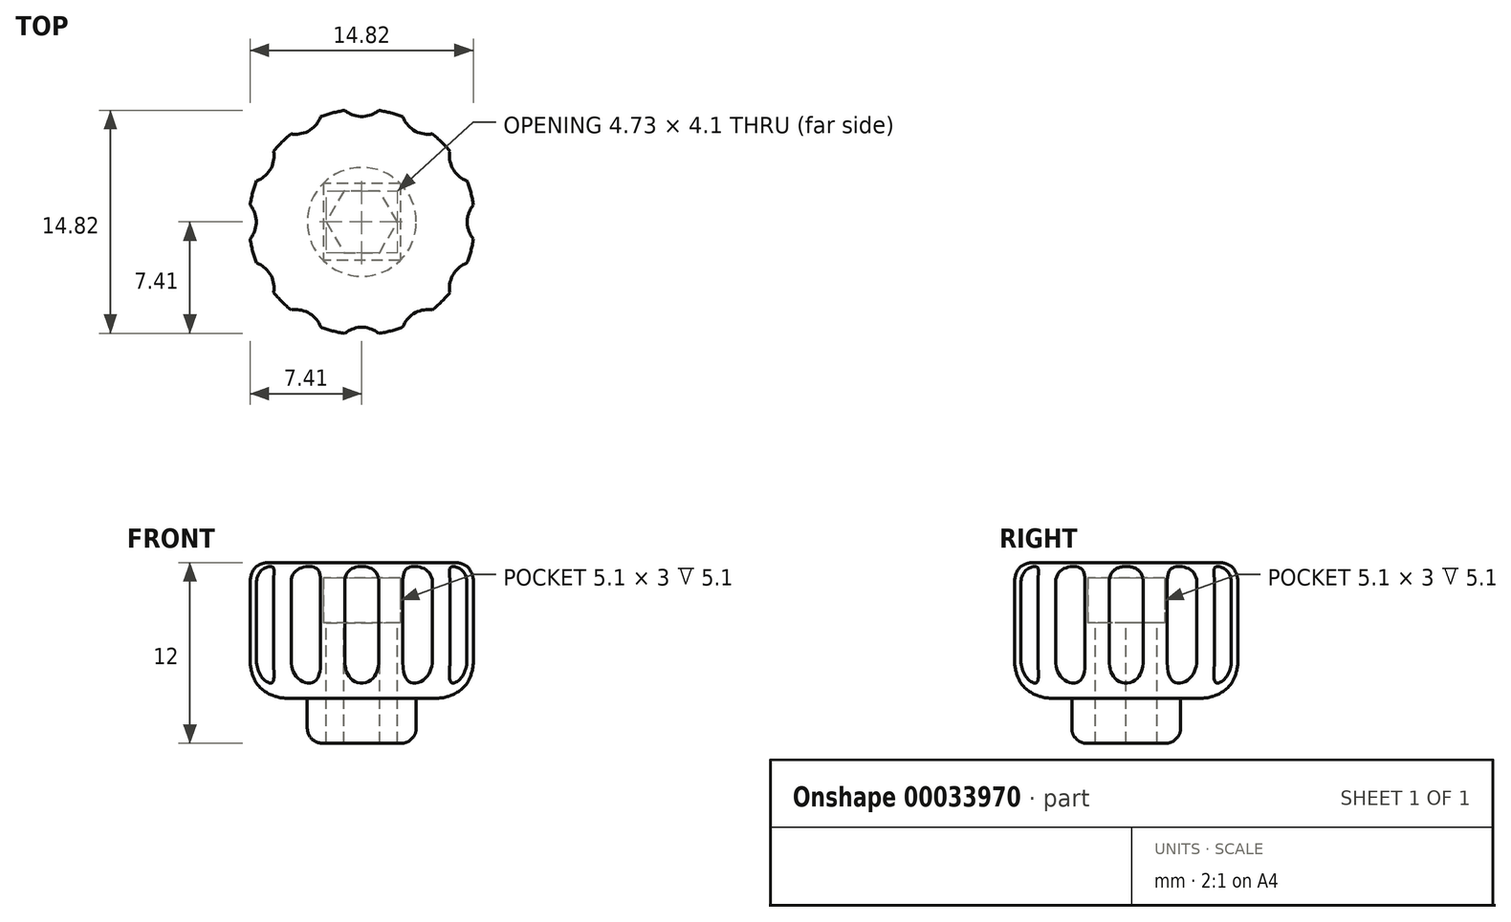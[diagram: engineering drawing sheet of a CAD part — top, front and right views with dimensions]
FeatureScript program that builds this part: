
annotation { "Feature Type Name" : "Feature", "Feature Type Description" : "" }
export const myFeature = defineFeature(function(context is Context, id is Id, definition is map)
    precondition{}
    {
        {
            var Q0;
            Q0=qCreatedBy(makeId("Top.planeOp"),FACE);
            var sketch = newSketch(context, id + "F0", { "sketchPlane" : qUnion([Q0])});
            skCircle(sketch, "E0", {"center": v(0, 0) * mm, "radius": 7.5 * mm});
            skLineSegment(sketch, "E1.rect.bottom", {"start": v(2.55, 2.55) * mm, "end": v(-2.55, 2.55) * mm});
            skLineSegment(sketch, "E1.rect.top", {"start": v(2.55, -2.55) * mm, "end": v(-2.55, -2.55) * mm});
            skLineSegment(sketch, "E1.rect.left", {"start": v(2.55, 2.55) * mm, "end": v(2.55, -2.55) * mm});
            skLineSegment(sketch, "E1.rect.right", {"start": v(-2.55, 2.55) * mm, "end": v(-2.55, -2.55) * mm});
            skSolve(sketch);
        }
        {
            var Q0;
            Q0=qCreatedBy(makeId("Right.planeOp"),FACE);
            var sketch = newSketch(context, id + "F1", { "sketchPlane" : qUnion([Q0])});
            skLineSegment(sketch, "E2", {"start": v(0, 0) * mm, "end": v(0, 13.29) * mm, "construction": true});
            skSolve(sketch);
        }
        {
            var Q0;
            Q0=makeQuery(id+"F0.imprint","IMPRINT",FACE,{"disambiguationData":[TD([[makeQuery(id+"F0.imprint","IMPRINT",EDGE,{"derivedFrom":sQuery(id+"F0.wireOp",EDGE,"E0")}),1.0]])]});
            extrude(context, id + "F2", {"entities" : qUnion([Q0]), "depth" : 3 * mm});
        }
        {
            var Q0;
            Q0=makeQuery(id+"F2.opExtrude","CAP_FACE",FACE,{"disambiguationData":[OSD([sQuery(id+"F0.wireOp",EDGE,"E0"),sQuery(id+"F0.wireOp",EDGE,"E1.rect.bottom"),sQuery(id+"F0.wireOp",EDGE,"E1.rect.top"),sQuery(id+"F0.wireOp",EDGE,"E1.rect.left"),sQuery(id+"F0.wireOp",EDGE,"E1.rect.right")])],"isStart":true});
            var sketch = newSketch(context, id + "F3", { "sketchPlane" : qUnion([Q0])});
            skCircle(sketch, "E3.0", {"center": v(0, 0) * mm, "radius": 7.5 * mm});
            skCircle(sketch, "E4.cCircle", {"center": v(0, 0) * mm, "radius": 2.37 * mm, "construction": true});
            skLineSegment(sketch, "E4.0", {"start": v(1.18, 2.05) * mm, "end": v(2.37, 0) * mm});
            skLineSegment(sketch, "E4.1", {"start": v(2.37, 0) * mm, "end": v(1.18, -2.05) * mm});
            skLineSegment(sketch, "E4.2", {"start": v(1.18, -2.05) * mm, "end": v(-1.18, -2.05) * mm});
            skLineSegment(sketch, "E4.3", {"start": v(-1.18, -2.05) * mm, "end": v(-2.37, 0) * mm});
            skLineSegment(sketch, "E4.4", {"start": v(-2.37, 0) * mm, "end": v(-1.18, 2.05) * mm});
            skLineSegment(sketch, "E4.5", {"start": v(-1.18, 2.05) * mm, "end": v(1.18, 2.05) * mm});
            skSolve(sketch);
        }
        {
            var Q0;
            {var subQ8=sQuery(id+"F3.wireOp",EDGE,"E4.2");Q0=makeQuery(id+"F3.imprint","IMPRINT",FACE,{"disambiguationData":[TD([[makeQuery(id+"F3.imprint","IMPRINT",EDGE,{"derivedFrom":subQ8}),1.0]])]});}
            var Q1;
            Q1=makeQuery(id+"F3.imprint","IMPRINT",FACE,{"disambiguationData":[TD([[makeQuery(id+"F3.imprint","IMPRINT",EDGE,{"derivedFrom":sQuery(id+"F3.wireOp",EDGE,"E3.0")}),-1.0]])]});
            extrude(context, id + "F4", {"entities" : qUnion([Q0, Q1]), "operationType" : NewBodyOperationType.ADD, "depth" : 5 * mm});
        }
        {
            var Q0;
            Q0=makeQuery(id+"F2.opExtrude","CAP_FACE",FACE,{"disambiguationData":[OSD([sQuery(id+"F0.wireOp",EDGE,"E0"),sQuery(id+"F0.wireOp",EDGE,"E1.rect.bottom"),sQuery(id+"F0.wireOp",EDGE,"E1.rect.top"),sQuery(id+"F0.wireOp",EDGE,"E1.rect.left"),sQuery(id+"F0.wireOp",EDGE,"E1.rect.right")])],"isStart":false});
            var sketch = newSketch(context, id + "F5", { "sketchPlane" : qUnion([Q0])});
            skCircle(sketch, "E5.0", {"center": v(0, 0) * mm, "radius": 7.5 * mm});
            skSolve(sketch);
        }
        {
            var Q0;
            Q0=makeQuery(id+"F5.imprint","IMPRINT",FACE,{"disambiguationData":[TD([[makeQuery(id+"F5.imprint","IMPRINT",EDGE,{"derivedFrom":makeQuery(id+"F2.opExtrude","CAP_EDGE",EDGE,{"disambiguationData":[OSD([sQuery(id+"F0.wireOp",EDGE,"E1.rect.bottom")])],"isStart":false})}),1.0]])]});
            var Q1;
            Q1=makeQuery(id+"F5.imprint","IMPRINT",FACE,{"disambiguationData":[TD([[makeQuery(id+"F5.imprint","IMPRINT",EDGE,{"derivedFrom":sQuery(id+"F5.wireOp",EDGE,"E5.0")}),1.0]])]});
            extrude(context, id + "F6", {"entities" : qUnion([Q0, Q1]), "operationType" : NewBodyOperationType.ADD, "depth" : 1 * mm});
        }
        {
            var Q0;
            Q0=makeQuery(id+"F4.opExtrude","CAP_EDGE",EDGE,{"disambiguationData":[OSD([sQuery(id+"F3.wireOp",EDGE,"E3.0")])],"isStart":false});
            fillet(context, id + "F7", {"entities" : qUnion([Q0]), "radius" : 2.5 * mm, "tangentPropagation" : true, "allowEdgeOverflow" : false});
        }
        {
            var Q0;
            Q0=makeQuery(id+"F6.opExtrude","CAP_FACE",FACE,{"disambiguationData":[OSD([sQuery(id+"F5.wireOp",EDGE,"E5.0")])],"isStart":false});
            var sketch = newSketch(context, id + "F8", { "sketchPlane" : qUnion([Q0])});
            skArc(sketch, "E6", {"start": v(-1.13, 7.41) * mm, "mid": v(0, 7) * mm, "end": v(1.13, 7.41) * mm});
            skArc(sketch, "E7.0", {"start": v(1.13, 7.41) * mm, "mid": v(0, 7.5) * mm, "end": v(-1.13, 7.41) * mm});
            skSolve(sketch);
        }
        {
            var Q0;
            Q0=makeQuery(id+"F6.opExtrude","CAP_EDGE",EDGE,{"disambiguationData":[OSD([sQuery(id+"F5.wireOp",EDGE,"E5.0")])],"isStart":false});
            fillet(context, id + "F9", {"entities" : qUnion([Q0]), "radius" : 1.25 * mm, "tangentPropagation" : true, "allowEdgeOverflow" : false});
        }
        {
            var Q0;
            Q0=makeQuery(id+"F8.imprint","IMPRINT",FACE,{"disambiguationData":[TD([[makeQuery(id+"F8.imprint","IMPRINT",EDGE,{"derivedFrom":sQuery(id+"F8.wireOp",EDGE,"E6")}),1.0]])]});
            extrude(context, id + "F10", {"entities" : qUnion([Q0]), "oppositeDirection" : true, "depth" : 25 * mm});
        }
        {
            var Q0;
            Q0=makeQuery(id+"F10.opExtrude","SWEPT_BODY",BODY,{"disambiguationData":[OSD([sQuery(id+"F8.wireOp",EDGE,"E6"),sQuery(id+"F8.wireOp",EDGE,"E7.0")])]});
            var Q1;
            Q1=sQuery(id+"F1.wireOp",EDGE,"E2");
            circularPattern(context, id + "F11", {"operationType" : NewBodyOperationType.REMOVE, "entities" : qUnion([Q0]), "axis" : qUnion([Q1]), "angle" : 30 * degree, "instanceCount" : 12});
        }
        {
            var Q0;
            Q0=makeQuery(id+"F4.opExtrude","CAP_FACE",FACE,{"disambiguationData":[OSD([sQuery(id+"F3.wireOp",EDGE,"E3.0"),sQuery(id+"F3.wireOp",EDGE,"E4.0"),sQuery(id+"F3.wireOp",EDGE,"E4.1"),sQuery(id+"F3.wireOp",EDGE,"E4.2"),sQuery(id+"F3.wireOp",EDGE,"E4.3"),sQuery(id+"F3.wireOp",EDGE,"E4.4"),sQuery(id+"F3.wireOp",EDGE,"E4.5")])],"isStart":false});
            var sketch = newSketch(context, id + "F12", { "sketchPlane" : qUnion([Q0])});
            skCircle(sketch, "E8", {"center": v(0, 0) * mm, "radius": 3.62 * mm});
            skSolve(sketch);
        }
        {
            var Q0;
            Q0=makeQuery(id+"F12.imprint","IMPRINT",FACE,{"disambiguationData":[TD([[makeQuery(id+"F12.imprint","IMPRINT",EDGE,{"derivedFrom":sQuery(id+"F12.wireOp",EDGE,"E8")}),1.0]])]});
            extrude(context, id + "F13", {"entities" : qUnion([Q0]), "operationType" : NewBodyOperationType.ADD, "depth" : 3 * mm});
        }
        {
            var Q0;
            Q0=makeQuery(id+"F13.opExtrude","CAP_EDGE",EDGE,{"disambiguationData":[OSD([sQuery(id+"F12.wireOp",EDGE,"E8")])],"isStart":false});
            fillet(context, id + "F14", {"entities" : qUnion([Q0]), "radius" : 1 * mm, "tangentPropagation" : true, "allowEdgeOverflow" : false});
        }
    });
